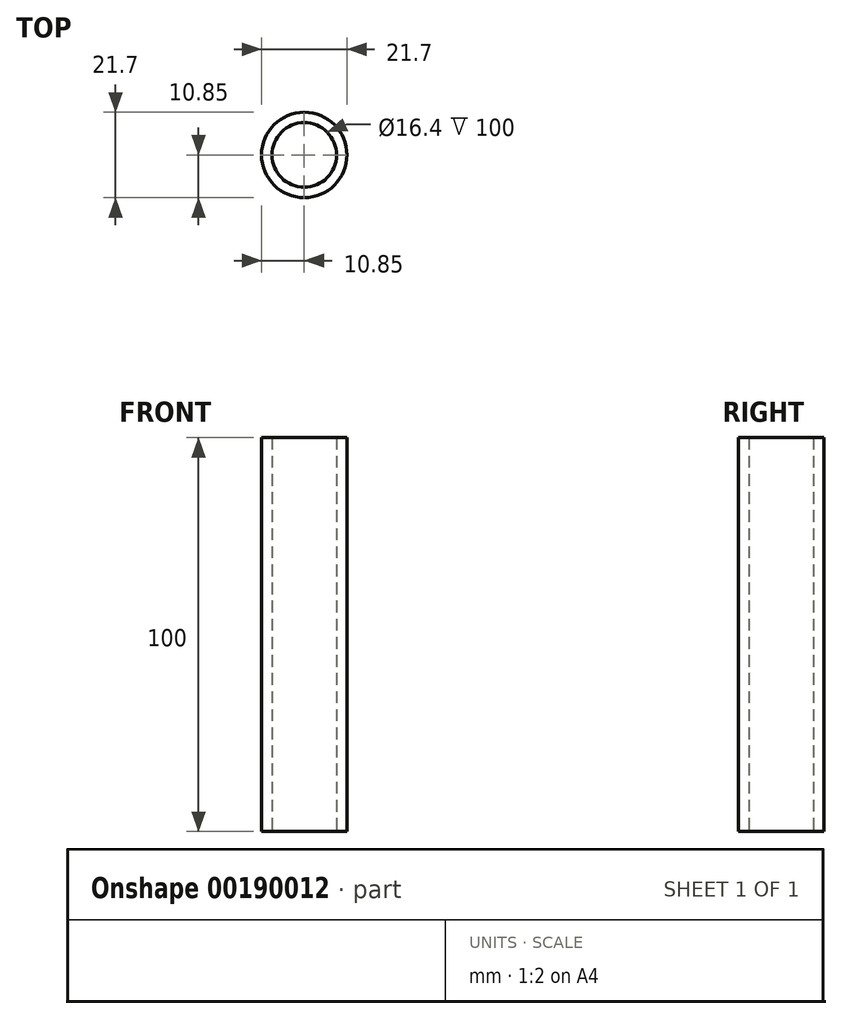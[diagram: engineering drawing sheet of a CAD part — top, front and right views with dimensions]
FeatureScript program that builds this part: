
annotation { "Feature Type Name" : "Feature", "Feature Type Description" : "" }
export const myFeature = defineFeature(function(context is Context, id is Id, definition is map)
    precondition{}
    {
        {
            var Q0;
            Q0=qCreatedBy(makeId("Top.planeOp"),FACE);
            var sketch = newSketch(context, id + "F0", { "sketchPlane" : qUnion([Q0])});
            skCircle(sketch, "E0", {"center": v(0, 0) * mm, "radius": 10.85 * mm});
            skCircle(sketch, "E1.0", {"center": v(0, 0) * mm, "radius": 8.2 * mm});
            skSolve(sketch);
        }
        {
            var Q0;
            Q0 = qSketchRegion(id + "F0", true);
            extrude(context, id + "F1", {"entities" : qUnion([Q0]), "depth" : 100 * mm});
        }
    });
